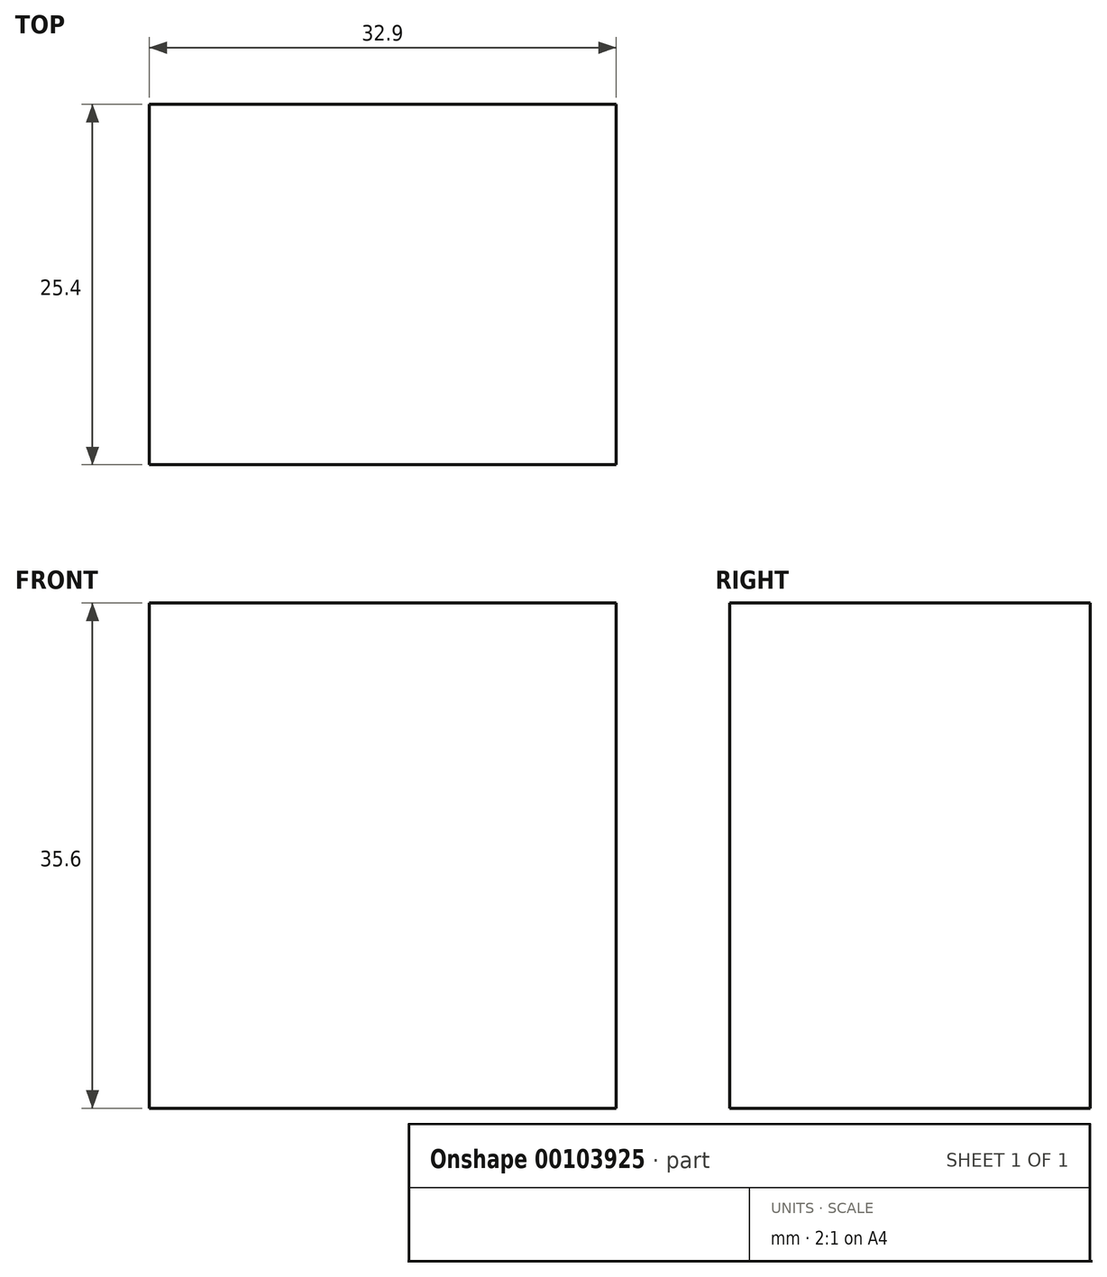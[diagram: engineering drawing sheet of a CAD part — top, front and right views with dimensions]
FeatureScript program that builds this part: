
annotation { "Feature Type Name" : "Feature", "Feature Type Description" : "" }
export const myFeature = defineFeature(function(context is Context, id is Id, definition is map)
    precondition{}
    {
        {
            var Q0;
            Q0=qCreatedBy(makeId("Front.planeOp"),FACE);
            var sketch = newSketch(context, id + "F0", { "sketchPlane" : qUnion([Q0])});
            skLineSegment(sketch, "E0.bottom", {"start": v(-13.16, 17.9) * mm, "end": v(19.74, 17.9) * mm});
            skLineSegment(sketch, "E0.top", {"start": v(-13.16, -17.7) * mm, "end": v(19.74, -17.7) * mm});
            skLineSegment(sketch, "E0.left", {"start": v(-13.16, 17.9) * mm, "end": v(-13.16, -17.7) * mm});
            skLineSegment(sketch, "E0.right", {"start": v(19.74, 17.9) * mm, "end": v(19.74, -17.7) * mm});
            skSolve(sketch);
        }
        {
            var Q0;
            Q0=makeQuery(id+"F0.imprint","IMPRINT",FACE,{"disambiguationData":[TD([[makeQuery(id+"F0.imprint","IMPRINT",EDGE,{"derivedFrom":sQuery(id+"F0.wireOp",EDGE,"E0.bottom")}),-1.0]])]});
            extrude(context, id + "F1", {"entities" : qUnion([Q0]), "depth" : 25.4 * mm});
        }
    });
